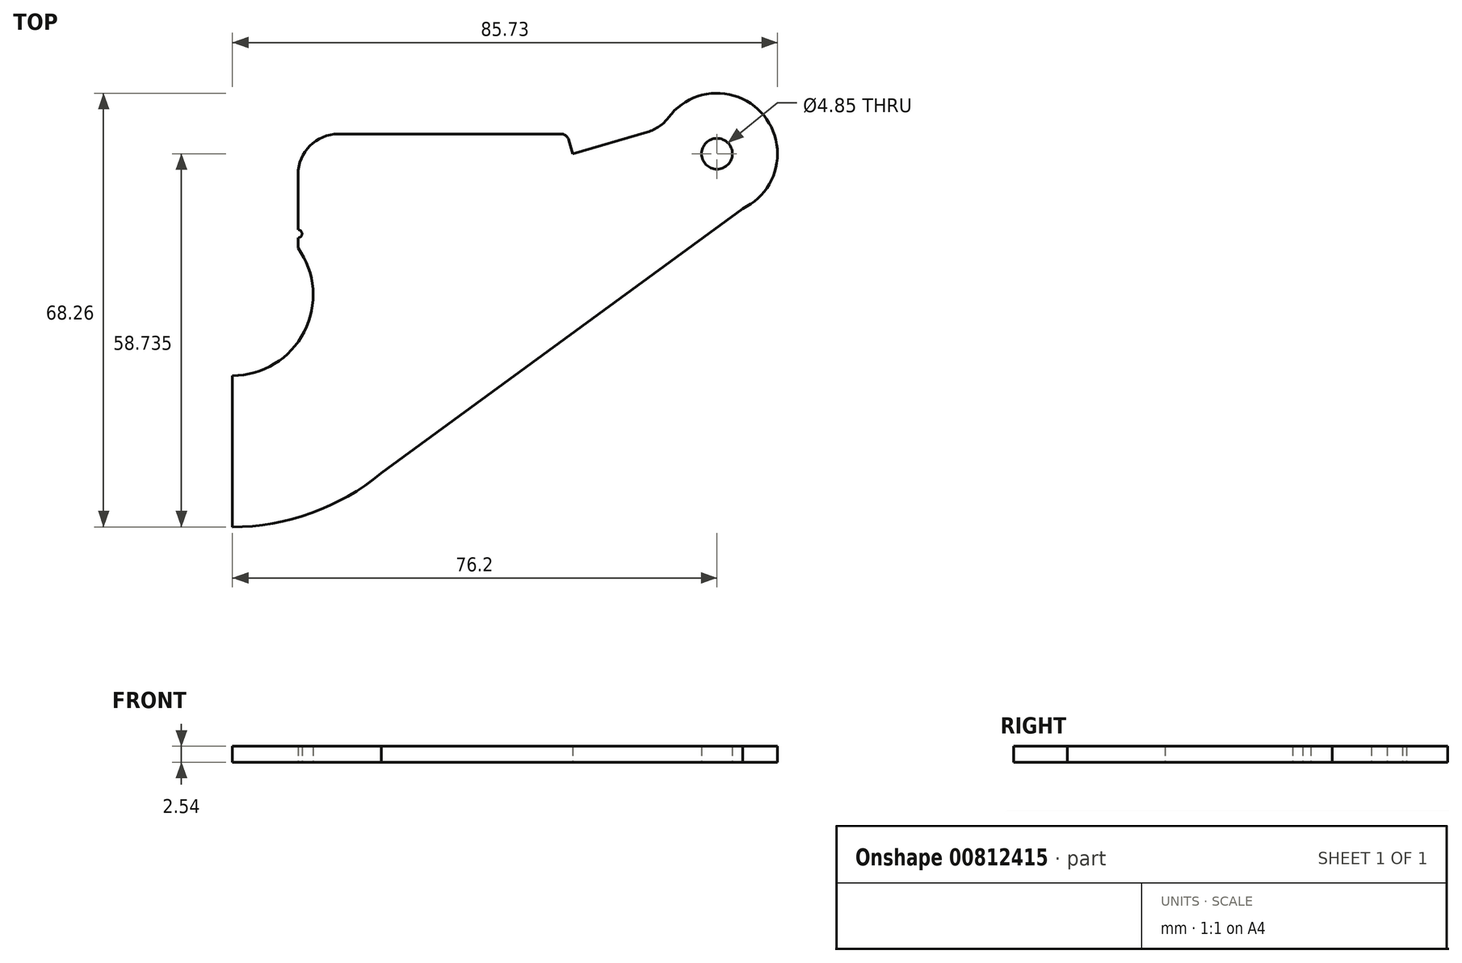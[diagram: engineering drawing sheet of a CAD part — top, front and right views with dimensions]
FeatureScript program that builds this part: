
annotation { "Feature Type Name" : "Feature", "Feature Type Description" : "" }
export const myFeature = defineFeature(function(context is Context, id is Id, definition is map)
    precondition{}
    {
        {
            var Q0;
            Q0=qCreatedBy(makeId("Top.planeOp"),FACE);
            var sketch = newSketch(context, id + "F0", { "sketchPlane" : qUnion([Q0])});
            skArc(sketch, "E0", {"start": v(-10.32, 7.4) * mm, "mid": v(0, -12.7) * mm, "end": v(10.32, 7.4) * mm});
            skCircle(sketch, "E1", {"center": v(-76.2, 22.23) * mm, "radius": 2.43 * mm});
            skCircle(sketch, "E2", {"center": v(76.2, 22.23) * mm, "radius": 2.43 * mm});
            skArc(sketch, "E3", {"start": v(-68.58, 27.94) * mm, "mid": v(-83.1, 28.8) * mm, "end": v(-81.53, 14.33) * mm});
            skArc(sketch, "E4", {"start": v(80.23, 13.6) * mm, "mid": v(83.6, 28.23) * mm, "end": v(68.58, 27.94) * mm});
            skArc(sketch, "E5", {"start": v(-24.33, -27.22) * mm, "mid": v(-0.62, -36.5) * mm, "end": v(23.39, -28.04) * mm});
            skLineSegment(sketch, "E6", {"start": v(-81.53, 14.33) * mm, "end": v(-24.33, -27.22) * mm});
            skLineSegment(sketch, "E7", {"start": v(23.39, -28.04) * mm, "end": v(83.2, 15.78) * mm});
            skLineSegment(sketch, "E8.0", {"start": v(-65.28, 25.65) * mm, "end": v(-53.54, 22.23) * mm});
            skLineSegment(sketch, "E9.0", {"start": v(53.54, 22.23) * mm, "end": v(65.28, 25.65) * mm});
            skLineSegment(sketch, "E10.left", {"start": v(10.32, 8.99) * mm, "end": v(10.32, 7.4) * mm});
            skLineSegment(sketch, "E10.right", {"start": v(-10.32, 9) * mm, "end": v(-10.32, 7.4) * mm});
            skPoint(sketch, "E10.top.end.orphan", {"position": v(-10.32, -39.66) * mm});
            skPoint(sketch, "E11.trimOffspring.end.orphan", {"position": v(10.32, -39.66) * mm});
            skPoint(sketch, "E10.bottom.end.orphan", {"position": v(-10.32, 39.66) * mm});
            skPoint(sketch, "E12.orphan", {"position": v(10.32, 39.66) * mm});
            skLineSegment(sketch, "E13", {"start": v(-10.32, 10.25) * mm, "end": v(-10.32, 18.98) * mm});
            skLineSegment(sketch, "E14", {"start": v(10.32, 10.26) * mm, "end": v(10.32, 18.98) * mm});
            skLineSegment(sketch, "E15", {"start": v(-52.9, 24.42) * mm, "end": v(-53.54, 22.23) * mm});
            skLineSegment(sketch, "E16", {"start": v(-16.67, 25.33) * mm, "end": v(-51.68, 25.33) * mm});
            skLineSegment(sketch, "E17", {"start": v(16.67, 25.33) * mm, "end": v(51.68, 25.33) * mm});
            skLineSegment(sketch, "E18", {"start": v(52.9, 24.42) * mm, "end": v(53.54, 22.23) * mm});
            skPoint(sketch, "E19.visualSharp", {"position": v(-67.6, 26.33) * mm});
            skArc(sketch, "E19.filletArc", {"start": v(-68.58, 27.94) * mm, "mid": v(-67.11, 26.53) * mm, "end": v(-65.28, 25.65) * mm});
            skPoint(sketch, "E20.visualSharp", {"position": v(67.6, 26.33) * mm});
            skArc(sketch, "E20.filletArc", {"start": v(65.28, 25.65) * mm, "mid": v(67.11, 26.53) * mm, "end": v(68.58, 27.94) * mm});
            skPoint(sketch, "E21.visualSharp", {"position": v(10.32, 25.33) * mm});
            skArc(sketch, "E21.filletArc", {"start": v(16.67, 25.33) * mm, "mid": v(12.18, 23.47) * mm, "end": v(10.32, 18.98) * mm});
            skPoint(sketch, "E22.visualSharp", {"position": v(-10.32, 25.33) * mm});
            skArc(sketch, "E22.filletArc", {"start": v(-10.32, 18.98) * mm, "mid": v(-12.18, 23.47) * mm, "end": v(-16.67, 25.33) * mm});
            skPoint(sketch, "E23.visualSharp", {"position": v(-52.63, 25.33) * mm});
            skArc(sketch, "E23.filletArc", {"start": v(-51.68, 25.33) * mm, "mid": v(-52.44, 25.08) * mm, "end": v(-52.9, 24.42) * mm});
            skPoint(sketch, "E24.visualSharp", {"position": v(52.64, 25.33) * mm});
            skArc(sketch, "E24.filletArc", {"start": v(52.9, 24.42) * mm, "mid": v(52.44, 25.08) * mm, "end": v(51.68, 25.33) * mm});
            skArc(sketch, "E25", {"start": v(-10.32, 10.25) * mm, "mid": v(-10.95, 9.62) * mm, "end": v(-10.32, 9) * mm});
            skArc(sketch, "E26", {"start": v(10.32, 8.99) * mm, "mid": v(10.95, 9.62) * mm, "end": v(10.32, 10.26) * mm});
            skSolve(sketch);
        }
        {
            var Q0;
            Q0=qSketchRegion(id+"F0",true);
            extrude(context, id + "F1", {"entities" : qUnion([Q0]), "depth" : 2.54 * mm, "offsetDistance" : 25.4 * mm});
        }
        {
            var Q0;
            Q0=qCreatedBy(makeId("Top.planeOp"),FACE);
            var sketch = newSketch(context, id + "F2", { "sketchPlane" : qUnion([Q0])});
            skLineSegment(sketch, "E27", {"start": v(0, 55.85) * mm, "end": v(0, -55.65) * mm});
            skLineSegment(sketch, "E28", {"start": v(0, -55.65) * mm, "end": v(-97.03, -55.65) * mm});
            skLineSegment(sketch, "E29", {"start": v(-97.03, -55.65) * mm, "end": v(-97.03, 55.85) * mm});
            skLineSegment(sketch, "E30", {"start": v(-97.03, 55.85) * mm, "end": v(0, 55.85) * mm});
            skSolve(sketch);
        }
        {
            var Q0;
            Q0 = qSketchRegion(id + "F2", true);
            extrude(context, id + "F3", {"entities" : qUnion([Q0]), "operationType" : NewBodyOperationType.REMOVE, "endBound" : BoundingType.SYMMETRIC, "oppositeDirection" : true, "depth" : 25.4 * mm, "offsetDistance" : 25.4 * mm});
        }
    });
